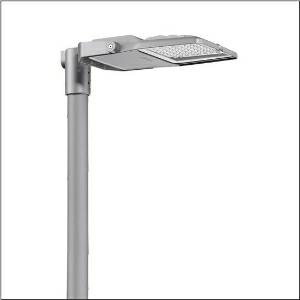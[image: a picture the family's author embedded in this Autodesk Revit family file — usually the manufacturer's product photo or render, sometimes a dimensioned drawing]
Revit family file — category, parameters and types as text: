
# Revit family: floodlight_fl_21_mini___pl33t_5xa7772c2f3a_7719
name_source: partatom
category: Lighting Fixtures
units: mm (PartAtom-declared; Revit-internal decimal feet)

## family parameters
Cut with Voids When Loaded = No
Host = Face
Light Source = No
Part Type = Normal
Room Calculation Point = No
Round Connector Dimension = Use Diameter
Shared = No

## types (1)
- --- (1 x LED, 12060 lm, 87.2 W, 3000K)
    Apparent Load = 87 VA
    CIE Flux Codes = 26 75 99 100 100
    Color Rendering = 70
    Color Temperature = 3000K
    Default Elevation = 1800 mm
    Description = Floodlight FL 21 mini, floodlight, primary light control with lens, of PMMA, primary optical cover: protective disc, of toughened safety glass, transparent, light distribution: PL33T, light emission: direct distribution, installation type: surface-mounted, LED, High Power LED, rated luminous flux: 12.060lm, luminous efficacy: 138lm/W, light colour: 730, colour temperature: 3000K, control gear: ECG iQ, control: Auto-Match, Temp-Guard, Night-Set, Smart-Wire, Desk-Remote (wireless, voltage-free reading and setting of iQ features in the workshop via application-optimized NFC function/RFID function), optimised constant luminous flux control (CLO 2.0), Light-Fading, Lumen-Switch, with terminal, 6-pole, mains connection: 220..240V, AC, 50/60Hz, start of lifetime: 87W, end of lifetime: 92W, reduction: 40W, luminaire housing, of diecast aluminium, powder-coated, Siteco® metallic grey (DB 702S), corrosivity category C5 according to DIN EN ISO 12944, mast bracket, of steel, galvanised, powder-coated, protection rating (complete): IP66, insulation class (complete): insulation class II (safety insulation), certification: CE, ENEC, VDE, protection symbol: D, impact resistance: IK08, permissible operating ambient temperature: -40..+40°C, permissible operating ambient temperature for outdoor applications: -40..+50°C, standard: DIN EN 12944, packaging unit: 1 piece

Light Distribution: PL33T
    Height = 70 mm
    Lamp = 1 x LED
    Lamp Light Flux = 12060 lm
    Lamp Power = 87.2 W
    Lamp count = 1
    Length = 485 mm
    Luminous efficacy = 138 lm/W
    Manufacturer = Siteco
    ModVariant = No
    Model = 5XA7772C2F3A
    Number of Poles = 1
    OnlyDefault = Yes
    Power Factor = 1
    Product Name = Floodlight FL 21 mini | PL33T
    Product group = floodlight | pylon top
    ProductGroupID = 6101
    Protection Class = Protection class II
    Protection Degree = IP 66
    RLX_Detail_Level = 1
    RlxData = <blob elided: 101069 chars, md5=ccc4d878>
    Socket = socket
    Standby Power = 0 W
    System Light Flux = 12060 lm
    System Power = 87 W
    Type Comments = factory setting: luminous flux: 100 % | dim-lin: 254 | 456 mA
    Type Image = l_1007125.jpg
    URL = http://relux.com
    VarID = @adj_059513
    Voltage = 0 V
    Weight = 0.00 kg
    Width = 337 mm

## geometry (parser evidence)
native form markers: Blend x4, Sweep x12
no freeform markers — native parametric forms only
